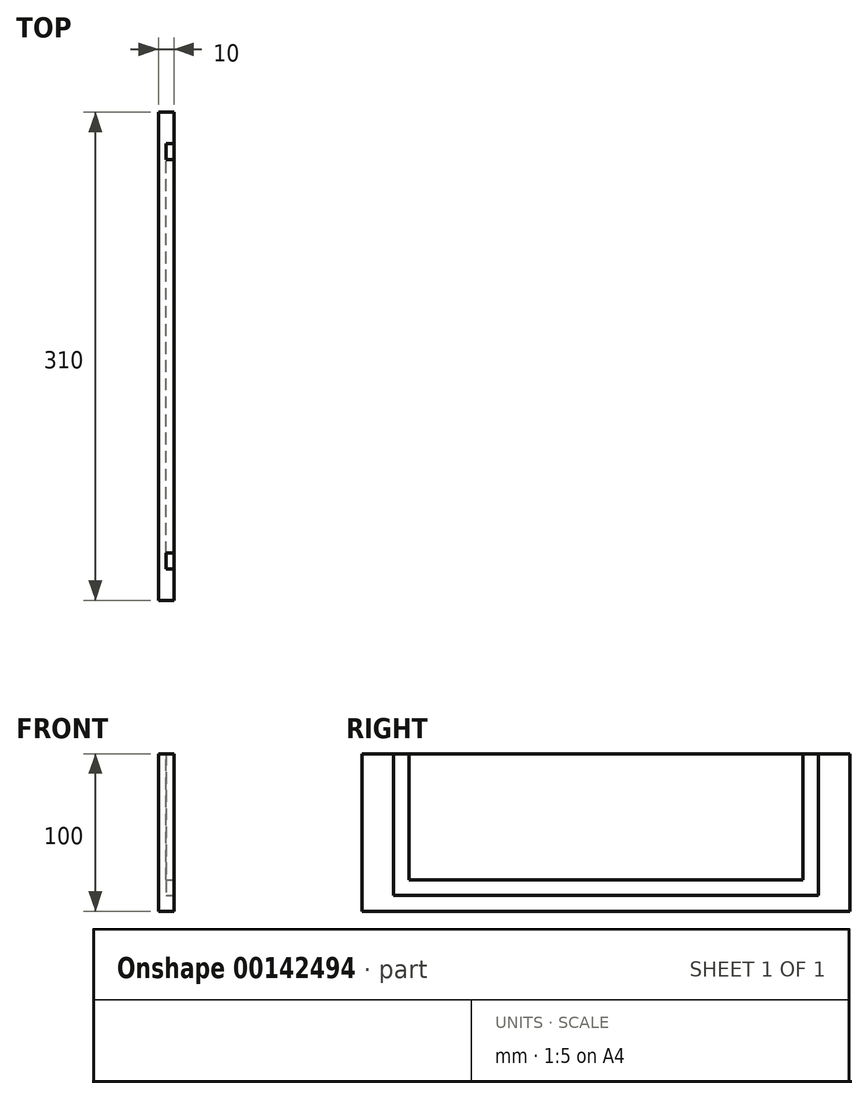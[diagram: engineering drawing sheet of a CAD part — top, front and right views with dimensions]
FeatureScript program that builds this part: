
annotation { "Feature Type Name" : "Feature", "Feature Type Description" : "" }
export const myFeature = defineFeature(function(context is Context, id is Id, definition is map)
    precondition{}
    {
        {
            var Q0;
            Q0=qCreatedBy(makeId("Right.planeOp"),FACE);
            var sketch = newSketch(context, id + "F0", { "sketchPlane" : qUnion([Q0])});
            skLineSegment(sketch, "E0.bottom", {"start": v(-155, 0) * mm, "end": v(155, 0) * mm});
            skLineSegment(sketch, "E0.top", {"start": v(-155, 100) * mm, "end": v(155, 100) * mm});
            skLineSegment(sketch, "E0.left", {"start": v(-155, 0) * mm, "end": v(-155, 100) * mm});
            skLineSegment(sketch, "E0.right", {"start": v(155, 0) * mm, "end": v(155, 100) * mm});
            skSolve(sketch);
        }
        {
            var Q0;
            Q0=makeQuery(id+"F0.imprint","IMPRINT",FACE,{"disambiguationData":[TD([[makeQuery(id+"F0.imprint","IMPRINT",EDGE,{"derivedFrom":sQuery(id+"F0.wireOp",EDGE,"E0.bottom")}),1.0]])]});
            extrude(context, id + "F1", {"entities" : qUnion([Q0]), "depth" : 10 * mm});
        }
        {
            var Q0;
            Q0=makeQuery(id+"F1.opExtrude","CAP_FACE",FACE,{"disambiguationData":[OSD([sQuery(id+"F0.wireOp",EDGE,"E0.bottom"),sQuery(id+"F0.wireOp",EDGE,"E0.top"),sQuery(id+"F0.wireOp",EDGE,"E0.left"),sQuery(id+"F0.wireOp",EDGE,"E0.right")])],"isStart":false});
            var sketch = newSketch(context, id + "F2", { "sketchPlane" : qUnion([Q0])});
            skLineSegment(sketch, "E1.bottom", {"start": v(-135, 100) * mm, "end": v(-125, 100) * mm});
            skLineSegment(sketch, "E1.left", {"start": v(-135, 100) * mm, "end": v(-135, 10) * mm});
            skLineSegment(sketch, "E2", {"start": v(0, 20) * mm, "end": v(-125, 20) * mm});
            skLineSegment(sketch, "E3", {"start": v(-125, 20) * mm, "end": v(-125, 100) * mm});
            skLineSegment(sketch, "E4", {"start": v(-135, 10) * mm, "end": v(0, 10) * mm});
            skLineSegment(sketch, "E5.MirrorCS", {"start": v(135, 10) * mm, "end": v(0, 10) * mm});
            skLineSegment(sketch, "E6.MirrorCS", {"start": v(135, 100) * mm, "end": v(135, 10) * mm});
            skLineSegment(sketch, "E7.MirrorCS", {"start": v(135, 100) * mm, "end": v(125, 100) * mm});
            skLineSegment(sketch, "E8.MirrorCS", {"start": v(125, 20) * mm, "end": v(125, 100) * mm});
            skLineSegment(sketch, "E9.MirrorCS", {"start": v(0, 20) * mm, "end": v(125, 20) * mm});
            skSolve(sketch);
        }
        {
            var Q0;
            Q0=makeQuery(id+"F2.imprint","IMPRINT",FACE,{"disambiguationData":[TD([[makeQuery(id+"F2.imprint","IMPRINT",EDGE,{"derivedFrom":sQuery(id+"F2.wireOp",EDGE,"E1.bottom")}),-1.0]])]});
            extrude(context, id + "F3", {"entities" : qUnion([Q0]), "operationType" : NewBodyOperationType.REMOVE, "oppositeDirection" : true, "depth" : 5 * mm});
        }
    });
